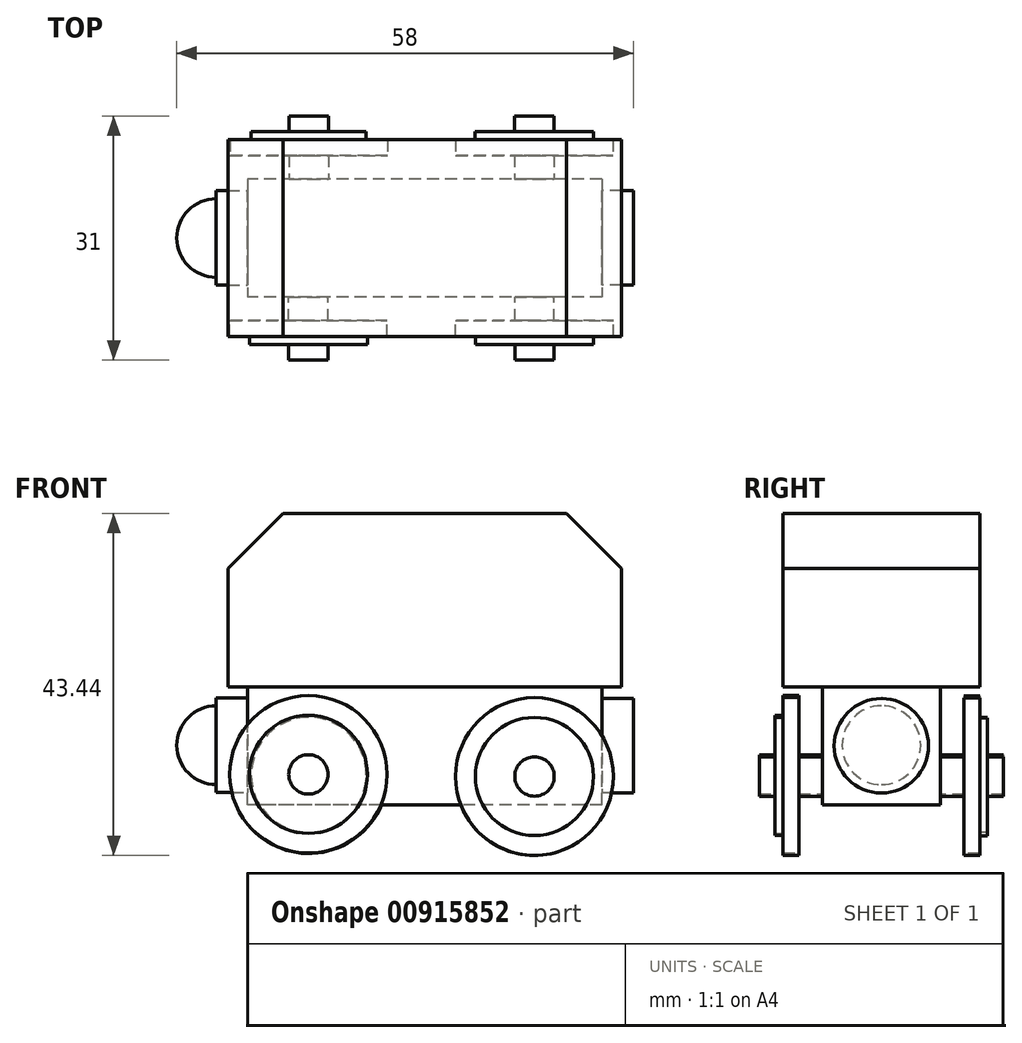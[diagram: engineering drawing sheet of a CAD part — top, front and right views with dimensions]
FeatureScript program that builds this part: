
annotation { "Feature Type Name" : "Feature", "Feature Type Description" : "" }
export const myFeature = defineFeature(function(context is Context, id is Id, definition is map)
    precondition{}
    {
        {
            var Q0;
            Q0=qCreatedBy(makeId("Front.planeOp"),FACE);
            var sketch = newSketch(context, id + "F0", { "sketchPlane" : qUnion([Q0])});
            skLineSegment(sketch, "E0.bottom", {"start": v(25, -11) * mm, "end": v(-25, -11) * mm});
            skLineSegment(sketch, "E0.top", {"start": v(25, 11) * mm, "end": v(-25, 11) * mm});
            skLineSegment(sketch, "E0.left", {"start": v(25, -11) * mm, "end": v(25, 11) * mm});
            skLineSegment(sketch, "E0.right", {"start": v(-25, -11) * mm, "end": v(-25, 11) * mm});
            skPoint(sketch, "E0.middle", {"position": v(0, 0) * mm});
            skSolve(sketch);
        }
        {
            var Q0;
            Q0=qSketchRegion(id+"F0",true);
            extrude(context, id + "F1", {"entities" : qUnion([Q0]), "endBound" : BoundingType.SYMMETRIC, "depth" : 25 * mm});
        }
        {
            var Q0;
            Q0=makeQuery(id+"F1.opExtrude","SWEPT_FACE",FACE,{"disambiguationData":[OSD([sQuery(id+"F0.wireOp",EDGE,"E0.bottom")])]});
            var sketch = newSketch(context, id + "F2", { "sketchPlane" : qUnion([Q0])});
            skLineSegment(sketch, "E1.bottom", {"start": v(22.5, -7.5) * mm, "end": v(-22.5, -7.5) * mm});
            skLineSegment(sketch, "E1.top", {"start": v(22.5, 7.5) * mm, "end": v(-22.5, 7.5) * mm});
            skLineSegment(sketch, "E1.left", {"start": v(22.5, -7.5) * mm, "end": v(22.5, 7.5) * mm});
            skLineSegment(sketch, "E1.right", {"start": v(-22.5, -7.5) * mm, "end": v(-22.5, 7.5) * mm});
            skPoint(sketch, "E1.middle", {"position": v(0, 0) * mm});
            skSolve(sketch);
        }
        {
            var Q0;
            Q0=makeQuery(id+"F2.imprint","IMPRINT",FACE,{"disambiguationData":[TD([[makeQuery(id+"F2.imprint","IMPRINT",EDGE,{"derivedFrom":sQuery(id+"F2.wireOp",EDGE,"E1.bottom")}),-1.0]])]});
            extrude(context, id + "F3", {"entities" : qUnion([Q0]), "operationType" : NewBodyOperationType.ADD, "depth" : 15 * mm});
        }
        {
            var Q0;
            Q0=makeQuery(id+"F3.opExtrude","SWEPT_FACE",FACE,{"disambiguationData":[OSD([sQuery(id+"F2.wireOp",EDGE,"E1.top")])]});
            var sketch = newSketch(context, id + "F4", { "sketchPlane" : qUnion([Q0])});
            skCircle(sketch, "E2", {"center": v(13.93, -22.4) * mm, "radius": 2.5 * mm});
            skSolve(sketch);
        }
        {
            var Q0;
            Q0=qSketchRegion(id+"F4",true);
            extrude(context, id + "F5", {"entities" : qUnion([Q0]), "operationType" : NewBodyOperationType.ADD, "depth" : 3 * mm});
        }
        {
            var Q0;
            Q0=makeQuery(id+"F3.opExtrude","SWEPT_FACE",FACE,{"disambiguationData":[OSD([sQuery(id+"F2.wireOp",EDGE,"E1.top")])]});
            var sketch = newSketch(context, id + "F6", { "sketchPlane" : qUnion([Q0])});
            skCircle(sketch, "E3", {"center": v(-14.78, -22.14) * mm, "radius": 2.5 * mm});
            skSolve(sketch);
        }
        {
            var Q0;
            Q0=qSketchRegion(id+"F6",true);
            extrude(context, id + "F7", {"entities" : qUnion([Q0]), "operationType" : NewBodyOperationType.ADD, "depth" : 3 * mm});
        }
        {
            var Q0;
            Q0=makeQuery(id+"F3.opExtrude","SWEPT_FACE",FACE,{"disambiguationData":[OSD([sQuery(id+"F2.wireOp",EDGE,"E1.bottom")])]});
            var sketch = newSketch(context, id + "F8", { "sketchPlane" : qUnion([Q0])});
            skCircle(sketch, "E4", {"center": v(14.74, -22.19) * mm, "radius": 2.5 * mm});
            skSolve(sketch);
        }
        {
            var Q0;
            Q0=qSketchRegion(id+"F8",true);
            extrude(context, id + "F9", {"entities" : qUnion([Q0]), "operationType" : NewBodyOperationType.ADD, "depth" : 3 * mm});
        }
        {
            var Q0;
            Q0=makeQuery(id+"F3.opExtrude","SWEPT_FACE",FACE,{"disambiguationData":[OSD([sQuery(id+"F2.wireOp",EDGE,"E1.bottom")])]});
            var sketch = newSketch(context, id + "F10", { "sketchPlane" : qUnion([Q0])});
            skCircle(sketch, "E5", {"center": v(-13.9, -22.44) * mm, "radius": 2.5 * mm});
            skSolve(sketch);
        }
        {
            var Q0;
            Q0=qSketchRegion(id+"F10",true);
            extrude(context, id + "F11", {"entities" : qUnion([Q0]), "operationType" : NewBodyOperationType.ADD, "depth" : 3 * mm});
        }
        {
            var Q0;
            Q0=makeQuery(id+"F11.opExtrude","CAP_FACE",FACE,{"disambiguationData":[OSD([sQuery(id+"F10.wireOp",EDGE,"E5")])],"isStart":false});
            var sketch = newSketch(context, id + "F12", { "sketchPlane" : qUnion([Q0])});
            skCircle(sketch, "E6", {"center": v(-13.9, -22.44) * mm, "radius": 10 * mm});
            skSolve(sketch);
        }
        {
            var Q0;
            Q0=qSketchRegion(id+"F12",true);
            extrude(context, id + "F13", {"entities" : qUnion([Q0]), "operationType" : NewBodyOperationType.ADD, "depth" : 2 * mm});
        }
        {
            var Q0;
            Q0=makeQuery(id+"F9.opExtrude","CAP_FACE",FACE,{"disambiguationData":[OSD([sQuery(id+"F8.wireOp",EDGE,"E4")])],"isStart":false});
            var sketch = newSketch(context, id + "F14", { "sketchPlane" : qUnion([Q0])});
            skCircle(sketch, "E7", {"center": v(14.74, -22.19) * mm, "radius": 10 * mm});
            skSolve(sketch);
        }
        {
            var Q0;
            Q0=qSketchRegion(id+"F14",true);
            extrude(context, id + "F15", {"entities" : qUnion([Q0]), "operationType" : NewBodyOperationType.ADD, "depth" : 2 * mm});
        }
        {
            var Q0;
            Q0=makeQuery(id+"F7.opExtrude","CAP_FACE",FACE,{"disambiguationData":[OSD([sQuery(id+"F6.wireOp",EDGE,"E3")])],"isStart":false});
            var sketch = newSketch(context, id + "F16", { "sketchPlane" : qUnion([Q0])});
            skCircle(sketch, "E8", {"center": v(-14.78, -22.14) * mm, "radius": 10 * mm});
            skSolve(sketch);
        }
        {
            var Q0;
            Q0=qSketchRegion(id+"F16",true);
            extrude(context, id + "F17", {"entities" : qUnion([Q0]), "operationType" : NewBodyOperationType.ADD, "depth" : 2 * mm});
        }
        {
            var Q0;
            Q0=makeQuery(id+"F5.opExtrude","CAP_FACE",FACE,{"disambiguationData":[OSD([sQuery(id+"F4.wireOp",EDGE,"E2")])],"isStart":false});
            var sketch = newSketch(context, id + "F18", { "sketchPlane" : qUnion([Q0])});
            skCircle(sketch, "E9", {"center": v(13.93, -22.4) * mm, "radius": 10.01 * mm});
            skSolve(sketch);
        }
        {
            var Q0;
            Q0=qSketchRegion(id+"F18",true);
            extrude(context, id + "F19", {"entities" : qUnion([Q0]), "operationType" : NewBodyOperationType.ADD, "depth" : 2 * mm});
        }
        {
            var Q0;
            Q0=makeQuery(id+"F17.opExtrude","CAP_FACE",FACE,{"disambiguationData":[OSD([sQuery(id+"F16.wireOp",EDGE,"E8")])],"isStart":false});
            var sketch = newSketch(context, id + "F20", { "sketchPlane" : qUnion([Q0])});
            skCircle(sketch, "E10", {"center": v(-14.78, -22.14) * mm, "radius": 7.5 * mm});
            skSolve(sketch);
        }
        {
            var Q0;
            Q0=qSketchRegion(id+"F20",true);
            extrude(context, id + "F21", {"entities" : qUnion([Q0]), "operationType" : NewBodyOperationType.ADD, "depth" : 1 * mm});
        }
        {
            var Q0;
            Q0=makeQuery(id+"F19.opExtrude","CAP_FACE",FACE,{"disambiguationData":[OSD([sQuery(id+"F18.wireOp",EDGE,"E9")])],"isStart":false});
            var sketch = newSketch(context, id + "F22", { "sketchPlane" : qUnion([Q0])});
            skCircle(sketch, "E11", {"center": v(13.93, -22.4) * mm, "radius": 7.5 * mm});
            skSolve(sketch);
        }
        {
            var Q0;
            Q0=makeQuery(id+"F22.imprint","IMPRINT",FACE,{"disambiguationData":[TD([[makeQuery(id+"F22.imprint","IMPRINT",EDGE,{"derivedFrom":sQuery(id+"F22.wireOp",EDGE,"E11")}),1.0]])]});
            extrude(context, id + "F23", {"entities" : qUnion([Q0]), "operationType" : NewBodyOperationType.ADD, "depth" : 1 * mm});
        }
        {
            var Q0;
            Q0=makeQuery(id+"F13.opExtrude","CAP_FACE",FACE,{"disambiguationData":[OSD([sQuery(id+"F12.wireOp",EDGE,"E6")])],"isStart":false});
            var sketch = newSketch(context, id + "F24", { "sketchPlane" : qUnion([Q0])});
            skCircle(sketch, "E12", {"center": v(-13.9, -22.44) * mm, "radius": 7.5 * mm});
            skSolve(sketch);
        }
        {
            var Q0;
            Q0=qSketchRegion(id+"F24",true);
            extrude(context, id + "F25", {"entities" : qUnion([Q0]), "operationType" : NewBodyOperationType.ADD, "depth" : 1 * mm});
        }
        {
            var Q0;
            Q0=makeQuery(id+"F15.opExtrude","CAP_FACE",FACE,{"disambiguationData":[OSD([sQuery(id+"F14.wireOp",EDGE,"E7")])],"isStart":false});
            var sketch = newSketch(context, id + "F26", { "sketchPlane" : qUnion([Q0])});
            skCircle(sketch, "E13", {"center": v(14.74, -22.19) * mm, "radius": 7.3 * mm});
            skSolve(sketch);
        }
        {
            var Q0;
            Q0=qSketchRegion(id+"F26",true);
            extrude(context, id + "F27", {"entities" : qUnion([Q0]), "operationType" : NewBodyOperationType.ADD, "depth" : 1 * mm});
        }
        {
            var Q0;
            Q0=makeQuery(id+"F25.opExtrude","CAP_FACE",FACE,{"disambiguationData":[OSD([sQuery(id+"F24.wireOp",EDGE,"E12")])],"isStart":false});
            var sketch = newSketch(context, id + "F28", { "sketchPlane" : qUnion([Q0])});
            skCircle(sketch, "E14", {"center": v(-13.9, -22.44) * mm, "radius": 2.5 * mm});
            skSolve(sketch);
        }
        {
            var Q0;
            Q0=qSketchRegion(id+"F28",true);
            extrude(context, id + "F29", {"entities" : qUnion([Q0]), "operationType" : NewBodyOperationType.ADD, "depth" : 2 * mm});
        }
        {
            var Q0;
            Q0=makeQuery(id+"F27.opExtrude","CAP_FACE",FACE,{"disambiguationData":[OSD([sQuery(id+"F26.wireOp",EDGE,"E13")])],"isStart":false});
            var sketch = newSketch(context, id + "F30", { "sketchPlane" : qUnion([Q0])});
            skCircle(sketch, "E15", {"center": v(14.74, -22.19) * mm, "radius": 2.5 * mm});
            skSolve(sketch);
        }
        {
            var Q0;
            Q0=qSketchRegion(id+"F30",true);
            extrude(context, id + "F31", {"entities" : qUnion([Q0]), "operationType" : NewBodyOperationType.ADD, "depth" : 2 * mm});
        }
        {
            var Q0;
            Q0=makeQuery(id+"F21.opExtrude","CAP_FACE",FACE,{"disambiguationData":[OSD([sQuery(id+"F20.wireOp",EDGE,"E10")])],"isStart":false});
            var sketch = newSketch(context, id + "F32", { "sketchPlane" : qUnion([Q0])});
            skCircle(sketch, "E16", {"center": v(-14.78, -22.14) * mm, "radius": 2.5 * mm});
            skSolve(sketch);
        }
        {
            var Q0;
            Q0=qSketchRegion(id+"F32",true);
            extrude(context, id + "F33", {"entities" : qUnion([Q0]), "operationType" : NewBodyOperationType.ADD, "depth" : 2 * mm});
        }
        {
            var Q0;
            Q0=makeQuery(id+"F23.opExtrude","CAP_FACE",FACE,{"disambiguationData":[OSD([sQuery(id+"F22.wireOp",EDGE,"E11")])],"isStart":false});
            var sketch = newSketch(context, id + "F34", { "sketchPlane" : qUnion([Q0])});
            skCircle(sketch, "E17", {"center": v(13.93, -22.4) * mm, "radius": 2.5 * mm});
            skSolve(sketch);
        }
        {
            var Q0;
            Q0=qSketchRegion(id+"F34",true);
            extrude(context, id + "F35", {"entities" : qUnion([Q0]), "operationType" : NewBodyOperationType.ADD, "depth" : 2 * mm});
        }
        {
            var Q0;
            Q0=makeQuery(id+"F3.opExtrude","SWEPT_FACE",FACE,{"disambiguationData":[OSD([sQuery(id+"F2.wireOp",EDGE,"E1.right")])]});
            var sketch = newSketch(context, id + "F36", { "sketchPlane" : qUnion([Q0])});
            skCircle(sketch, "E18", {"center": v(0, -18.44) * mm, "radius": 6 * mm});
            skSolve(sketch);
        }
        {
            var Q0;
            Q0=qSketchRegion(id+"F36",true);
            extrude(context, id + "F37", {"entities" : qUnion([Q0]), "operationType" : NewBodyOperationType.ADD, "depth" : 4 * mm});
        }
        {
            var Q0;
            Q0=makeQuery(id+"F3.opExtrude","SWEPT_FACE",FACE,{"disambiguationData":[OSD([sQuery(id+"F2.wireOp",EDGE,"E1.left")])]});
            var sketch = newSketch(context, id + "F38", { "sketchPlane" : qUnion([Q0])});
            skCircle(sketch, "E19", {"center": v(0, -18.5) * mm, "radius": 6 * mm});
            skSolve(sketch);
        }
        {
            var Q0;
            Q0=qSketchRegion(id+"F38",true);
            extrude(context, id + "F39", {"entities" : qUnion([Q0]), "operationType" : NewBodyOperationType.ADD, "depth" : 4 * mm});
        }
        {
            var Q0;
            Q0=makeQuery(id+"F37.opExtrude","CAP_FACE",FACE,{"disambiguationData":[OSD([sQuery(id+"F36.wireOp",EDGE,"E18")])],"isStart":false});
            var sketch = newSketch(context, id + "F40", { "sketchPlane" : qUnion([Q0])});
            skPoint(sketch, "E20", {"position": v(0, -18.44) * mm});
            skArc(sketch, "E21", {"start": v(0, -13.44) * mm, "mid": v(-5, -18.44) * mm, "end": v(0, -23.44) * mm});
            skLineSegment(sketch, "E22", {"start": v(0, -13.44) * mm, "end": v(0, -23.44) * mm});
            skSolve(sketch);
        }
        {
            var Q0;
            Q0=makeQuery(id+"F40.imprint","IMPRINT",FACE,{"disambiguationData":[TD([[makeQuery(id+"F40.imprint","IMPRINT",EDGE,{"derivedFrom":sQuery(id+"F40.wireOp",EDGE,"E21")}),1.0]])]});
            var Q1;
            Q1=sQuery(id+"F40.wireOp",EDGE,"E22");
            revolve(context, id + "F41", {"operationType" : NewBodyOperationType.ADD, "entities" : qUnion([Q0]), "axis" : qUnion([Q1]), "revolveType" : RevolveType.FULL});
        }
        {
            var Q0;
            Q0=makeQuery(id+"F1.opExtrude","SWEPT_EDGE",EDGE,{"disambiguationData":[OSD([sQuery(id+"F0.wireOp",EDGE,"E0.top"),sQuery(id+"F0.wireOp",EDGE,"E0.right")])]});
            chamfer(context, id + "F42", {"entities" : qUnion([Q0]), "width" : 7 * mm, "tangentPropagation" : true});
        }
        {
            var Q0;
            Q0=makeQuery(id+"F1.opExtrude","SWEPT_EDGE",EDGE,{"disambiguationData":[OSD([sQuery(id+"F0.wireOp",EDGE,"E0.top"),sQuery(id+"F0.wireOp",EDGE,"E0.left")])]});
            chamfer(context, id + "F43", {"entities" : qUnion([Q0]), "width" : 7 * mm, "tangentPropagation" : true});
        }
    });
